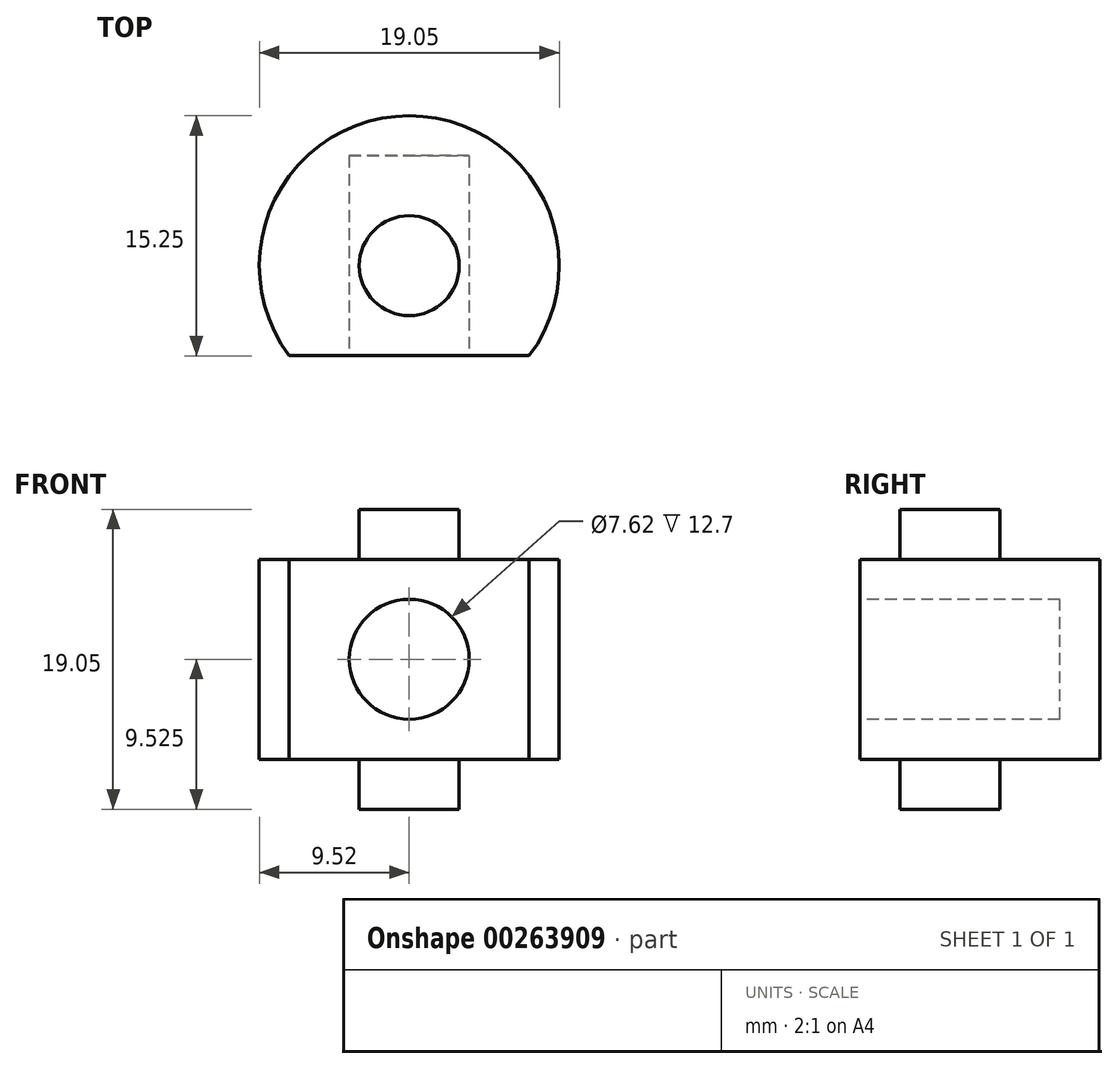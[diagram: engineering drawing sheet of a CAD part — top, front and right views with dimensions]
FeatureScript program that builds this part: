
annotation { "Feature Type Name" : "Feature", "Feature Type Description" : "" }
export const myFeature = defineFeature(function(context is Context, id is Id, definition is map)
    precondition{}
    {
        {
            var Q0;
            Q0=qCreatedBy(makeId("Top.planeOp"),FACE);
            var sketch = newSketch(context, id + "F0", { "sketchPlane" : qUnion([Q0])});
            skCircle(sketch, "E0", {"center": v(0, 0) * mm, "radius": 3.18 * mm});
            skSolve(sketch);
        }
        {
            var Q0;
            Q0 = qSketchRegion(id + "F0", true);
            extrude(context, id + "F1", {"entities" : qUnion([Q0]), "depth" : 3.17 * mm});
        }
        {
            var Q0;
            Q0=makeQuery(id+"F1.opExtrude","CAP_FACE",FACE,{"disambiguationData":[OSD([sQuery(id+"F0.wireOp",EDGE,"E0")])],"isStart":false});
            var sketch = newSketch(context, id + "F2", { "sketchPlane" : qUnion([Q0])});
            skCircle(sketch, "E1", {"center": v(0, 0) * mm, "radius": 9.53 * mm});
            skLineSegment(sketch, "E2", {"start": v(7.62, -5.71) * mm, "end": v(-7.62, -5.72) * mm});
            skSolve(sketch);
        }
        {
            var Q0;
            Q0=makeQuery(id+"F2.imprint","IMPRINT",FACE,{"disambiguationData":[TD([[makeQuery(id+"F2.imprint","IMPRINT",EDGE,{"derivedFrom":makeQuery(id+"F1.opExtrude","CAP_EDGE",EDGE,{"disambiguationData":[OSD([sQuery(id+"F0.wireOp",EDGE,"E0")])],"isStart":false})}),1.0]])]});
            var Q1;
            {var subQ0=sQuery(id+"F2.wireOp",EDGE,"E2");Q1=makeQuery(id+"F2.imprint","IMPRINT",FACE,{"disambiguationData":[TD([[makeQuery(id+"F2.imprint","IMPRINT",EDGE,{"derivedFrom":subQ0}),-1.0]])]});}
            extrude(context, id + "F3", {"entities" : qUnion([Q0, Q1]), "operationType" : NewBodyOperationType.ADD, "depth" : 12.7 * mm});
        }
        {
            var Q0;
            Q0=makeQuery(id+"F3.opExtrude","CAP_FACE",FACE,{"disambiguationData":[OSD([sQuery(id+"F2.wireOp",EDGE,"E1")])],"isStart":false});
            var sketch = newSketch(context, id + "F4", { "sketchPlane" : qUnion([Q0])});
            skCircle(sketch, "E3", {"center": v(0, 0) * mm, "radius": 3.18 * mm});
            skSolve(sketch);
        }
        {
            var Q0;
            Q0 = qSketchRegion(id + "F4", true);
            extrude(context, id + "F5", {"entities" : qUnion([Q0]), "operationType" : NewBodyOperationType.ADD, "depth" : 3.17 * mm});
        }
        {
            var Q0;
            Q0=makeQuery(id+"F3.opExtrude","SWEPT_FACE",FACE,{"disambiguationData":[OSD([sQuery(id+"F2.wireOp",EDGE,"E2")])]});
            var sketch = newSketch(context, id + "F6", { "sketchPlane" : qUnion([Q0])});
            skCircle(sketch, "E4", {"center": v(0, 9.53) * mm, "radius": 3.81 * mm});
            skPoint(sketch, "E4.centerSnap0", {"position": v(-7.62, 9.53) * mm});
            skPoint(sketch, "E4.centerSnap1", {"position": v(0, 15.88) * mm});
            skSolve(sketch);
        }
        {
            var Q0;
            Q0 = qSketchRegion(id + "F6", true);
            extrude(context, id + "F7", {"entities" : qUnion([Q0]), "operationType" : NewBodyOperationType.REMOVE, "oppositeDirection" : true, "depth" : 12.7 * mm});
        }
    });
